# Revit family: CL 20 (a)
name_source: partatom
category: Equipement spécialisé
revit_build: Autodesk Revit LT 2015 (Build: 20140606_1530(x64)
units: mm (PartAtom-declared; Revit-internal decimal feet)

## types (3) — shared parameters
Apparent Power = 0 VA
Description = COUPE-LEGUMES
Electrique connexion = 40 mm  [stored 0.131234 ft]
Fabricant = ROBOT COUPE
Height = 565 mm
Modèle = CL 20
Phase = 1
Speeds (Rpm) = 1500
UP Height = 660 mm
UP Width = 407 mm
URL = www.robot-coupe.com
Watts = 400 W
Weight = 12 kg
Width = 332 mm
water = Connector
zero-valued in all types: Cold water supply, Cold water supply height, Top, Used water, Waste water height

## per-type parameters (varying)
| type | Cycle | Depth | Volts |
| CL 20  230/50/1 | 50 Hz | 304 mm  [stored 0.997375 ft] | 230 V |
| CL 20  120/60/1 | 60 Hz | 302 mm | 120 V |
| CL 20  220/60/1 | 60 Hz | 302 mm | 220 V |

note: [stored X ft] marks values corroborated as IEEE doubles in the binary element streams (Revit-internal decimal feet)

## geometry (parser evidence)
native form markers: Blend x104, Sweep x5
no freeform markers — native parametric forms only
